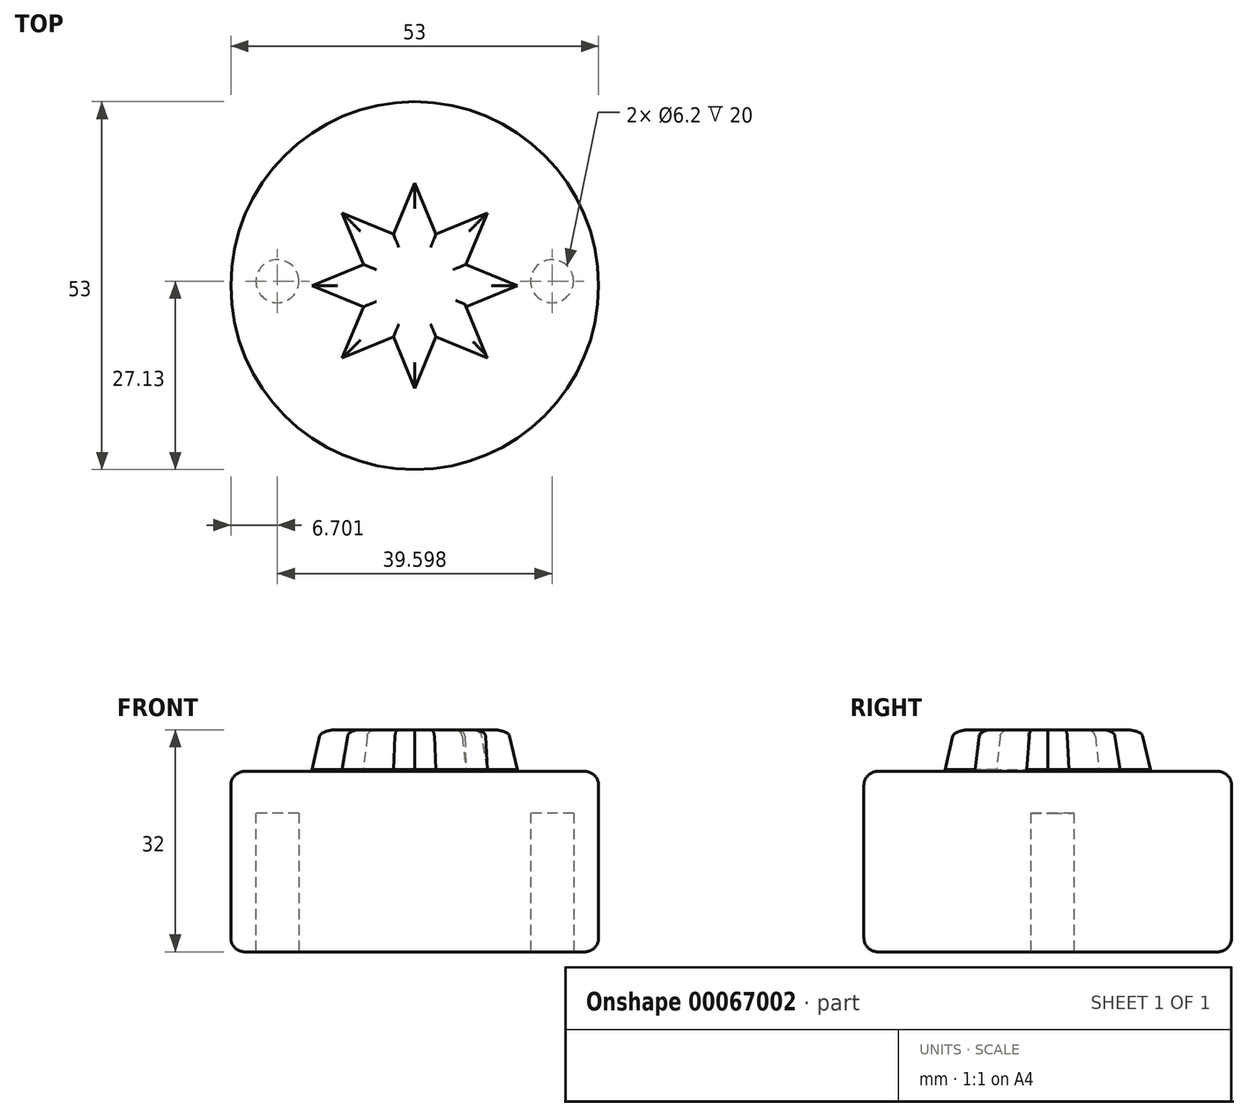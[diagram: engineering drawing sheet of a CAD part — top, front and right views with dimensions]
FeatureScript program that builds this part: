
annotation { "Feature Type Name" : "Feature", "Feature Type Description" : "" }
export const myFeature = defineFeature(function(context is Context, id is Id, definition is map)
    precondition{}
    {
        {
            var Q0;
            Q0=qCreatedBy(makeId("Top.planeOp"),FACE);
            var sketch = newSketch(context, id + "F0", { "sketchPlane" : qUnion([Q0])});
            skCircle(sketch, "E0", {"center": v(-19.8, 0.63) * mm, "radius": 3.1 * mm});
            skCircle(sketch, "E1", {"center": v(19.8, 0.63) * mm, "radius": 3.1 * mm});
            skLineSegment(sketch, "E2", {"start": v(-19.8, 0.63) * mm, "end": v(19.8, 0.63) * mm, "construction": true});
            skCircle(sketch, "E3", {"center": v(0, 0) * mm, "radius": 26.5 * mm});
            skSolve(sketch);
        }
        {
            var Q0;
            Q0 = qSketchRegion(id + "F0", true);
            extrude(context, id + "F1", {"entities" : qUnion([Q0]), "depth" : 20 * mm});
        }
        {
            var Q0;
            Q0=makeQuery(id+"F1.opExtrude","CAP_FACE",FACE,{"disambiguationData":[OSD([sQuery(id+"F0.wireOp",EDGE,"E0"),sQuery(id+"F0.wireOp",EDGE,"E1"),sQuery(id+"F0.wireOp",EDGE,"E3")])],"isStart":false});
            var sketch = newSketch(context, id + "F2", { "sketchPlane" : qUnion([Q0])});
            skCircle(sketch, "E4", {"center": v(0, 0) * mm, "radius": 26.5 * mm});
            skSolve(sketch);
        }
        {
            var Q0;
            Q0 = qSketchRegion(id + "F2", true);
            extrude(context, id + "F3", {"entities" : qUnion([Q0]), "operationType" : NewBodyOperationType.ADD, "depth" : 6 * mm});
        }
        {
            var Q0;
            Q0=makeQuery(id+"F3.opExtrude","CAP_EDGE",EDGE,{"disambiguationData":[OSD([sQuery(id+"F2.wireOp",EDGE,"E4")])],"isStart":false});
            var Q1;
            Q1=makeQuery(id+"F1.opExtrude","CAP_EDGE",EDGE,{"disambiguationData":[OSD([sQuery(id+"F0.wireOp",EDGE,"E3")])],"isStart":true});
            fillet(context, id + "F4", {"entities" : qUnion([Q0, Q1]), "radius" : 2 * mm, "tangentPropagation" : true, "allowEdgeOverflow" : false});
        }
        {
            var Q0;
            Q0=makeQuery(id+"F3.opExtrude","CAP_FACE",FACE,{"disambiguationData":[OSD([sQuery(id+"F2.wireOp",EDGE,"E4")])],"isStart":false});
            var sketch = newSketch(context, id + "F5", { "sketchPlane" : qUnion([Q0])});
            skLineSegment(sketch, "E5", {"start": v(-3.06, 7.4) * mm, "end": v(0, 14.78) * mm});
            skLineSegment(sketch, "E6", {"start": v(0, 14.78) * mm, "end": v(3.06, 7.4) * mm});
            skLineSegment(sketch, "E7", {"start": v(-3.06, 7.4) * mm, "end": v(0, 0) * mm, "construction": true});
            skLineSegment(sketch, "E8", {"start": v(3.06, 7.4) * mm, "end": v(0, 0) * mm, "construction": true});
            skLineSegment(sketch, "E9.1.0", {"start": v(-10.45, 10.45) * mm, "end": v(-3.06, 7.4) * mm});
            skLineSegment(sketch, "E9.1.1", {"start": v(-7.4, 3.06) * mm, "end": v(0, 0) * mm, "construction": true});
            skLineSegment(sketch, "E9.1.2", {"start": v(-7.4, 3.06) * mm, "end": v(-10.45, 10.45) * mm});
            skLineSegment(sketch, "E9.2.0", {"start": v(-14.78, 0) * mm, "end": v(-7.4, 3.06) * mm});
            skLineSegment(sketch, "E9.2.1", {"start": v(-7.4, -3.06) * mm, "end": v(0, 0) * mm, "construction": true});
            skLineSegment(sketch, "E9.2.2", {"start": v(-7.4, -3.06) * mm, "end": v(-14.78, 0) * mm});
            skLineSegment(sketch, "E9.2.3", {"start": v(-7.4, 3.06) * mm, "end": v(0, 0) * mm, "construction": true});
            skLineSegment(sketch, "E9.3.0", {"start": v(-10.45, -10.45) * mm, "end": v(-7.4, -3.06) * mm});
            skLineSegment(sketch, "E9.3.1", {"start": v(-3.06, -7.4) * mm, "end": v(0, 0) * mm, "construction": true});
            skLineSegment(sketch, "E9.3.2", {"start": v(-3.06, -7.4) * mm, "end": v(-10.45, -10.45) * mm});
            skLineSegment(sketch, "E9.3.3", {"start": v(-7.4, -3.06) * mm, "end": v(0, 0) * mm, "construction": true});
            skLineSegment(sketch, "E9.4.0", {"start": v(0, -14.78) * mm, "end": v(-3.06, -7.4) * mm});
            skLineSegment(sketch, "E9.4.1", {"start": v(3.06, -7.4) * mm, "end": v(0, 0) * mm, "construction": true});
            skLineSegment(sketch, "E9.4.2", {"start": v(3.06, -7.4) * mm, "end": v(0, -14.78) * mm});
            skLineSegment(sketch, "E9.4.3", {"start": v(-3.06, -7.4) * mm, "end": v(0, 0) * mm, "construction": true});
            skLineSegment(sketch, "E9.5.0", {"start": v(10.45, -10.45) * mm, "end": v(3.06, -7.4) * mm});
            skLineSegment(sketch, "E9.5.1", {"start": v(7.4, -3.06) * mm, "end": v(0, 0) * mm, "construction": true});
            skLineSegment(sketch, "E9.5.2", {"start": v(7.4, -3.06) * mm, "end": v(10.45, -10.45) * mm});
            skLineSegment(sketch, "E9.5.3", {"start": v(3.06, -7.4) * mm, "end": v(0, 0) * mm, "construction": true});
            skLineSegment(sketch, "E9.6.0", {"start": v(14.78, 0) * mm, "end": v(7.4, -3.06) * mm});
            skLineSegment(sketch, "E9.6.1", {"start": v(7.4, 3.06) * mm, "end": v(0, 0) * mm, "construction": true});
            skLineSegment(sketch, "E9.6.2", {"start": v(7.4, 3.06) * mm, "end": v(14.78, 0) * mm});
            skLineSegment(sketch, "E9.6.3", {"start": v(7.4, -3.06) * mm, "end": v(0, 0) * mm, "construction": true});
            skLineSegment(sketch, "E9.7.0", {"start": v(10.45, 10.45) * mm, "end": v(7.4, 3.06) * mm});
            skLineSegment(sketch, "E9.7.2", {"start": v(3.06, 7.4) * mm, "end": v(10.45, 10.45) * mm});
            skLineSegment(sketch, "E9.7.3", {"start": v(7.4, 3.06) * mm, "end": v(0, 0) * mm, "construction": true});
            skPoint(sketch, "E9.center", {"position": v(0, 0) * mm});
            skLineSegment(sketch, "E9.anchor1", {"start": v(0, 0) * mm, "end": v(-3.06, 7.4) * mm, "construction": true});
            skLineSegment(sketch, "E9.anchor2", {"start": v(0, 0) * mm, "end": v(3.06, 7.4) * mm, "construction": true});
            skSolve(sketch);
        }
        {
            var Q0;
            Q0 = qSketchRegion(id + "F5", true);
            extrude(context, id + "F6", {"entities" : qUnion([Q0]), "operationType" : NewBodyOperationType.ADD, "depth" : 6 * mm});
        }
        {
            var Q0;
            Q0=makeQuery(id+"F6.opExtrude","CAP_EDGE",EDGE,{"disambiguationData":[OSD([sQuery(id+"F5.wireOp",EDGE,"E9.5.0")])],"isStart":false});
            var Q1;
            Q1=makeQuery(id+"F6.opExtrude","CAP_EDGE",EDGE,{"disambiguationData":[OSD([sQuery(id+"F5.wireOp",EDGE,"E9.4.0")])],"isStart":false});
            var Q2;
            Q2=makeQuery(id+"F6.opExtrude","CAP_EDGE",EDGE,{"disambiguationData":[OSD([sQuery(id+"F5.wireOp",EDGE,"E9.3.0")])],"isStart":false});
            var Q3;
            Q3=makeQuery(id+"F6.opExtrude","CAP_EDGE",EDGE,{"disambiguationData":[OSD([sQuery(id+"F5.wireOp",EDGE,"E9.2.0")])],"isStart":false});
            var Q4;
            Q4=makeQuery(id+"F6.opExtrude","CAP_EDGE",EDGE,{"disambiguationData":[OSD([sQuery(id+"F5.wireOp",EDGE,"E9.1.0")])],"isStart":false});
            var Q5;
            Q5=makeQuery(id+"F6.opExtrude","CAP_EDGE",EDGE,{"disambiguationData":[OSD([sQuery(id+"F5.wireOp",EDGE,"E6")])],"isStart":false});
            var Q6;
            Q6=makeQuery(id+"F6.opExtrude","CAP_EDGE",EDGE,{"disambiguationData":[OSD([sQuery(id+"F5.wireOp",EDGE,"E9.7.0")])],"isStart":false});
            var Q7;
            Q7=makeQuery(id+"F6.opExtrude","CAP_EDGE",EDGE,{"disambiguationData":[OSD([sQuery(id+"F5.wireOp",EDGE,"E9.6.0")])],"isStart":false});
            chamfer(context, id + "F7", {"entities" : qUnion([Q0, Q1, Q2, Q3, Q4, Q5, Q6, Q7]), "chamferType" : ChamferType.OFFSET_ANGLE, "width" : 0.5 * mm, "oppositeDirection" : true, "angle" : 85 * degree, "tangentPropagation" : true});
        }
        {
            var Q0;
            Q0=makeQuery(id+"F6.opExtrude","CAP_EDGE",EDGE,{"disambiguationData":[OSD([sQuery(id+"F5.wireOp",EDGE,"E9.4.2")])],"isStart":false});
            var Q1;
            Q1=makeQuery(id+"F6.opExtrude","CAP_EDGE",EDGE,{"disambiguationData":[OSD([sQuery(id+"F5.wireOp",EDGE,"E9.3.2")])],"isStart":false});
            var Q2;
            Q2=makeQuery(id+"F6.opExtrude","CAP_EDGE",EDGE,{"disambiguationData":[OSD([sQuery(id+"F5.wireOp",EDGE,"E9.2.2")])],"isStart":false});
            var Q3;
            Q3=makeQuery(id+"F6.opExtrude","CAP_EDGE",EDGE,{"disambiguationData":[OSD([sQuery(id+"F5.wireOp",EDGE,"E9.1.2")])],"isStart":false});
            var Q4;
            Q4=makeQuery(id+"F6.opExtrude","CAP_EDGE",EDGE,{"disambiguationData":[OSD([sQuery(id+"F5.wireOp",EDGE,"E5")])],"isStart":false});
            var Q5;
            Q5=makeQuery(id+"F6.opExtrude","CAP_EDGE",EDGE,{"disambiguationData":[OSD([sQuery(id+"F5.wireOp",EDGE,"E9.7.2")])],"isStart":false});
            var Q6;
            Q6=makeQuery(id+"F6.opExtrude","CAP_EDGE",EDGE,{"disambiguationData":[OSD([sQuery(id+"F5.wireOp",EDGE,"E9.6.2")])],"isStart":false});
            chamfer(context, id + "F8", {"entities" : qUnion([Q0, Q1, Q2, Q3, Q4, Q5, Q6]), "chamferType" : ChamferType.OFFSET_ANGLE, "width" : 0.5 * mm, "oppositeDirection" : true, "angle" : 85 * degree, "tangentPropagation" : true});
        }
        {
            var Q0;
            Q0=makeQuery(id+"F6.opExtrude","CAP_FACE",FACE,{"disambiguationData":[OSD([sQuery(id+"F5.wireOp",EDGE,"E5"),sQuery(id+"F5.wireOp",EDGE,"E6"),sQuery(id+"F5.wireOp",EDGE,"E9.1.0"),sQuery(id+"F5.wireOp",EDGE,"E9.1.2"),sQuery(id+"F5.wireOp",EDGE,"E9.2.0"),sQuery(id+"F5.wireOp",EDGE,"E9.2.2"),sQuery(id+"F5.wireOp",EDGE,"E9.3.0"),sQuery(id+"F5.wireOp",EDGE,"E9.3.2"),sQuery(id+"F5.wireOp",EDGE,"E9.4.0"),sQuery(id+"F5.wireOp",EDGE,"E9.4.2"),sQuery(id+"F5.wireOp",EDGE,"E9.5.0"),sQuery(id+"F5.wireOp",EDGE,"E9.5.2"),sQuery(id+"F5.wireOp",EDGE,"E9.6.0"),sQuery(id+"F5.wireOp",EDGE,"E9.6.2"),sQuery(id+"F5.wireOp",EDGE,"E9.7.0"),sQuery(id+"F5.wireOp",EDGE,"E9.7.2")])],"isStart":false});
            fillet(context, id + "F9", {"entities" : qUnion([Q0]), "radius" : 1 * mm, "tangentPropagation" : true, "allowEdgeOverflow" : false});
        }
    });
